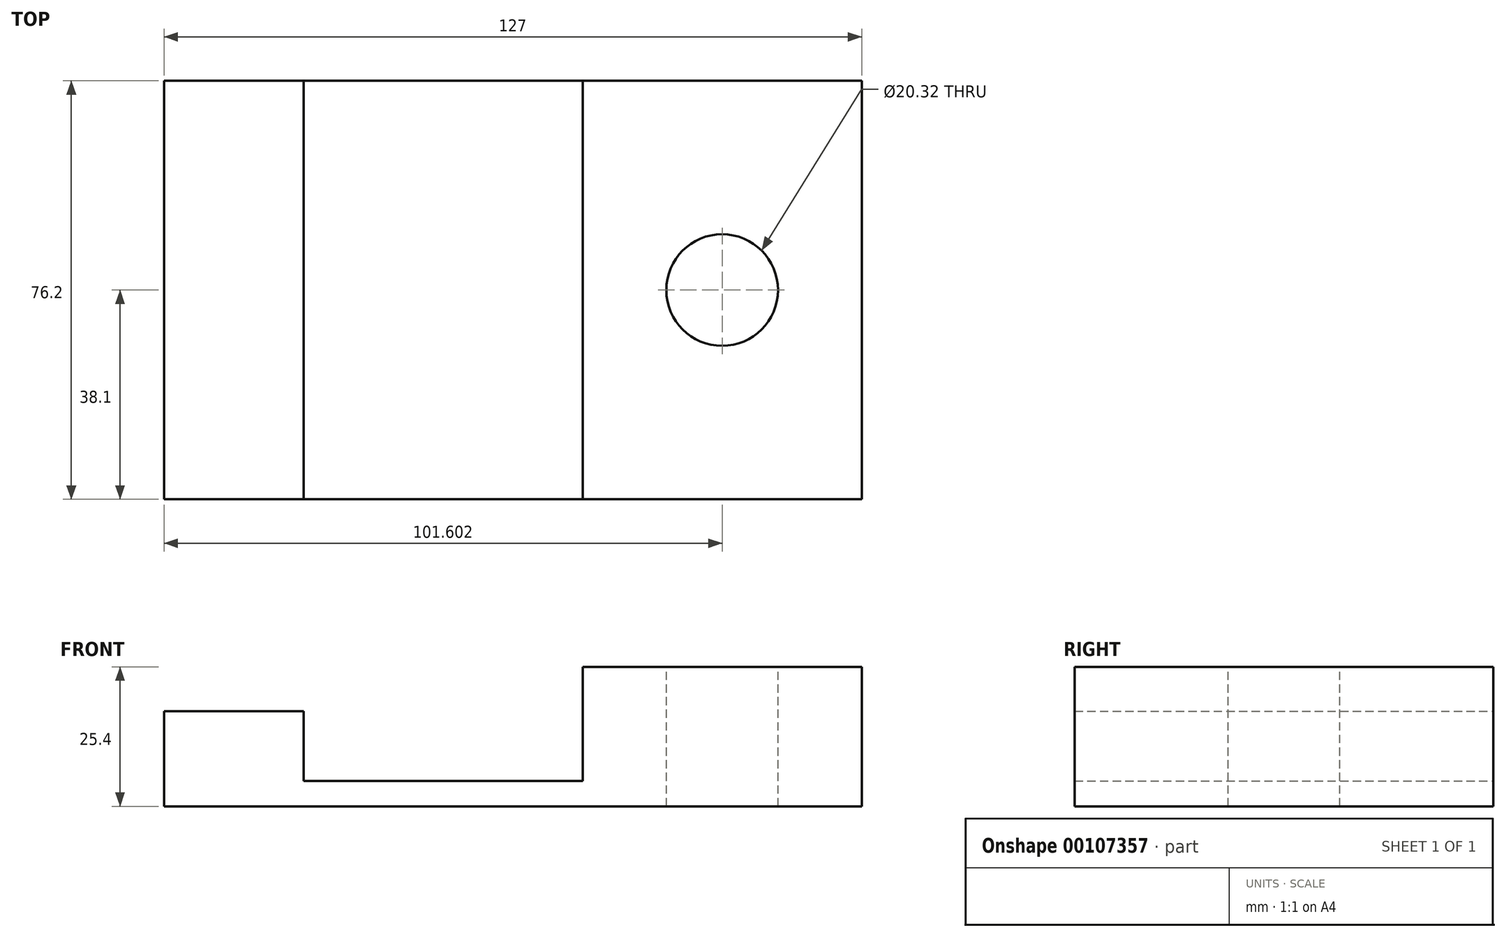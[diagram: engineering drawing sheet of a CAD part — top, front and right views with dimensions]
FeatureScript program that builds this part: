
annotation { "Feature Type Name" : "Feature", "Feature Type Description" : "" }
export const myFeature = defineFeature(function(context is Context, id is Id, definition is map)
    precondition{}
    {
        {
            var Q0;
            Q0=qCreatedBy(makeId("Front.planeOp"),FACE);
            var sketch = newSketch(context, id + "F0", { "sketchPlane" : qUnion([Q0])});
            skLineSegment(sketch, "E0", {"start": v(-48.15, 12.7) * mm, "end": v(-48.15, -4.6) * mm});
            skLineSegment(sketch, "E1", {"start": v(-48.15, -4.6) * mm, "end": v(78.85, -4.6) * mm});
            skLineSegment(sketch, "E2", {"start": v(78.85, -4.6) * mm, "end": v(78.85, 20.8) * mm});
            skLineSegment(sketch, "E3", {"start": v(78.85, 20.8) * mm, "end": v(28.05, 20.8) * mm});
            skLineSegment(sketch, "E4", {"start": v(-48.15, 12.7) * mm, "end": v(-22.75, 12.7) * mm});
            skLineSegment(sketch, "E5", {"start": v(-22.75, 12.7) * mm, "end": v(-22.75, 0) * mm});
            skLineSegment(sketch, "E6", {"start": v(-22.75, 0) * mm, "end": v(28.05, 0) * mm});
            skLineSegment(sketch, "E7", {"start": v(28.05, 0) * mm, "end": v(28.05, 20.8) * mm});
            skSolve(sketch);
        }
        {
            var Q0;
            Q0 = qSketchRegion(id + "F0", true);
            extrude(context, id + "F1", {"entities" : qUnion([Q0]), "endBound" : BoundingType.SYMMETRIC, "depth" : 76.2 * mm});
        }
        {
            var Q0;
            Q0=makeQuery(id+"F1.opExtrude","SWEPT_FACE",FACE,{"disambiguationData":[OSD([sQuery(id+"F0.wireOp",EDGE,"E3")])]});
            var sketch = newSketch(context, id + "F2", { "sketchPlane" : qUnion([Q0])});
            skCircle(sketch, "E8", {"center": v(53.45, 0) * mm, "radius": 10.16 * mm});
            skSolve(sketch);
        }
        {
            var Q0;
            Q0=sQuery(id+"F2.wireOp",VERTEX,"E8.center");
            var Q1;
            Q1=makeQuery(id+"F1.opExtrude","SWEPT_BODY",BODY,{"disambiguationData":[OSD([sQuery(id+"F0.wireOp",EDGE,"E0"),sQuery(id+"F0.wireOp",EDGE,"E1"),sQuery(id+"F0.wireOp",EDGE,"E2"),sQuery(id+"F0.wireOp",EDGE,"E3"),sQuery(id+"F0.wireOp",EDGE,"E4"),sQuery(id+"F0.wireOp",EDGE,"E5"),sQuery(id+"F0.wireOp",EDGE,"E6"),sQuery(id+"F0.wireOp",EDGE,"E7")])]});
            hole(context, id + "F3", {"style" : HoleStyle.SIMPLE, "endStyle" : HoleEndStyle.THROUGH, "holeDiameter" : 20.32 * mm, "locations" : qUnion([Q0]), "scope" : qUnion([Q1]), "isTappedThrough" : true});
        }
    });
